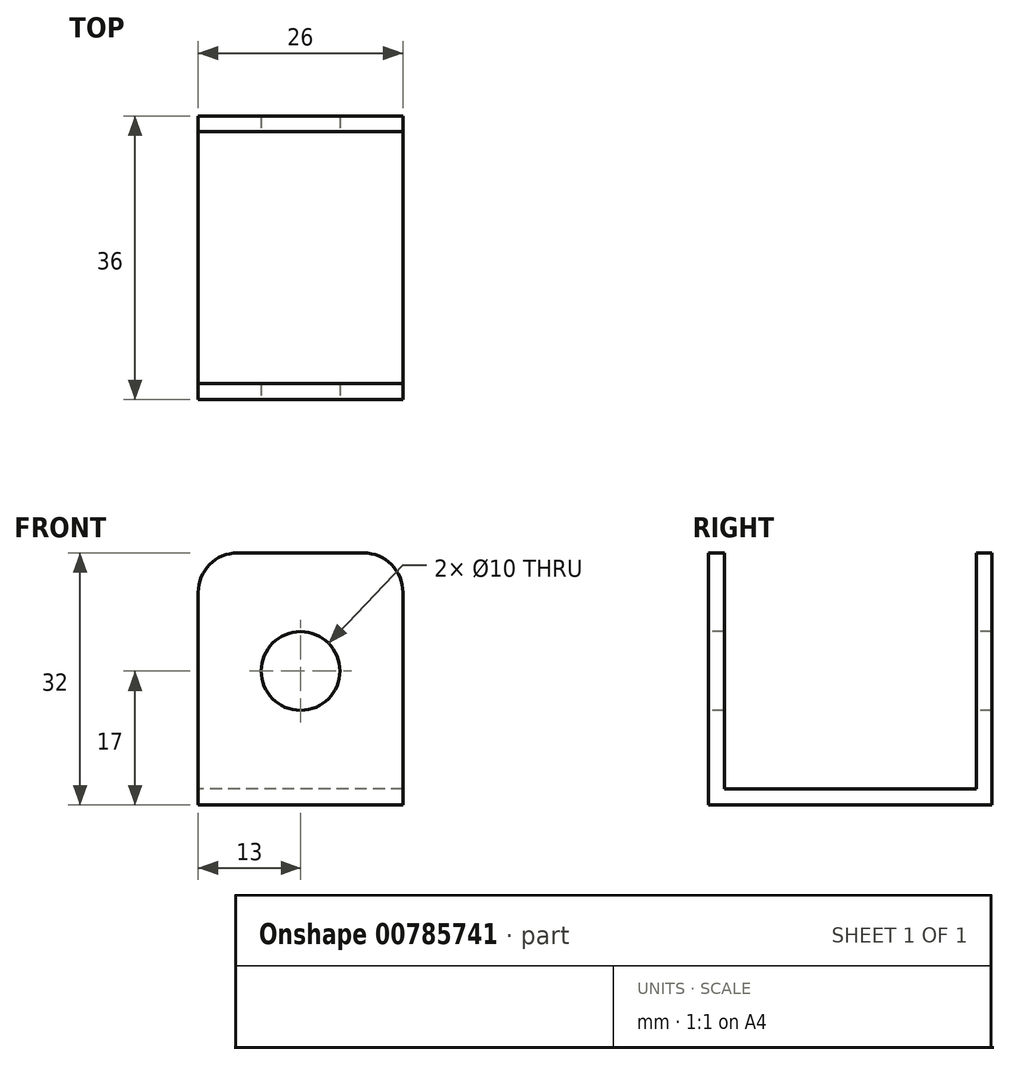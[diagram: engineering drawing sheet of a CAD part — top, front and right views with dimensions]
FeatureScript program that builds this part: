
annotation { "Feature Type Name" : "Feature", "Feature Type Description" : "" }
export const myFeature = defineFeature(function(context is Context, id is Id, definition is map)
    precondition{}
    {
        {
            var Q0;
            Q0=qCreatedBy(makeId("Right.planeOp"),FACE);
            var sketch = newSketch(context, id + "F0", { "sketchPlane" : qUnion([Q0])});
            skLineSegment(sketch, "E0.bottom", {"start": v(-1, 15) * mm, "end": v(1, 15) * mm});
            skLineSegment(sketch, "E0.top", {"start": v(-1, -15) * mm, "end": v(1, -15) * mm});
            skLineSegment(sketch, "E0.left", {"start": v(-1, 15) * mm, "end": v(-1, -15) * mm});
            skLineSegment(sketch, "E0.right", {"start": v(1, 15) * mm, "end": v(1, -15) * mm});
            skPoint(sketch, "E0.middle", {"position": v(0, 0) * mm});
            skLineSegment(sketch, "E1.bottom", {"start": v(-1, -15) * mm, "end": v(35, -15) * mm});
            skLineSegment(sketch, "E1.top", {"start": v(-1, -17) * mm, "end": v(35, -17) * mm});
            skLineSegment(sketch, "E1.left", {"start": v(-1, -15) * mm, "end": v(-1, -17) * mm});
            skLineSegment(sketch, "E1.right", {"start": v(35, -15) * mm, "end": v(35, -17) * mm});
            skLineSegment(sketch, "E2.bottom", {"start": v(35, -15) * mm, "end": v(33, -15) * mm});
            skLineSegment(sketch, "E2.top", {"start": v(35, 15) * mm, "end": v(33, 15) * mm});
            skLineSegment(sketch, "E2.left", {"start": v(35, -15) * mm, "end": v(35, 15) * mm});
            skLineSegment(sketch, "E2.right", {"start": v(33, -15) * mm, "end": v(33, 15) * mm});
            skSolve(sketch);
        }
        {
            var Q0;
            Q0=qSketchRegion(id+"F0",true);
            extrude(context, id + "F1", {"entities" : qUnion([Q0]), "depth" : 26 * mm, "offsetDistance" : 25 * mm});
        }
        {
            var Q0;
            Q0=qCreatedBy(makeId("Front.planeOp"),FACE);
            var sketch = newSketch(context, id + "F2", { "sketchPlane" : qUnion([Q0])});
            skCircle(sketch, "E3", {"center": v(13, 0) * mm, "radius": 5 * mm});
            skSolve(sketch);
        }
        {
            var Q0;
            Q0=qSketchRegion(id+"F2",true);
            extrude(context, id + "F3", {"entities" : qUnion([Q0]), "operationType" : NewBodyOperationType.REMOVE, "oppositeDirection" : true, "depth" : 40.2 * mm, "offsetDistance" : 25 * mm});
        }
        {
            var Q0;
            Q0=qCreatedBy(makeId("Front.planeOp"),FACE);
            var sketch = newSketch(context, id + "F4", { "sketchPlane" : qUnion([Q0])});
            skCircle(sketch, "E4", {"center": v(13, 0) * mm, "radius": 5 * mm});
            skSolve(sketch);
        }
        {
            var Q0;
            Q0=qSketchRegion(id+"F4",true);
            extrude(context, id + "F5", {"entities" : qUnion([Q0]), "operationType" : NewBodyOperationType.REMOVE, "depth" : 23 * mm, "offsetDistance" : 25 * mm});
        }
        {
            var Q0;
            Q0=makeQuery(id+"F1.opExtrude","CAP_EDGE",EDGE,{"disambiguationData":[OSD([sQuery(id+"F0.wireOp",EDGE,"E0.bottom")])],"isStart":false});
            var Q1;
            Q1=makeQuery(id+"F1.opExtrude","CAP_EDGE",EDGE,{"disambiguationData":[OSD([sQuery(id+"F0.wireOp",EDGE,"E2.top")])],"isStart":false});
            var Q2;
            Q2=makeQuery(id+"F1.opExtrude","CAP_EDGE",EDGE,{"disambiguationData":[OSD([sQuery(id+"F0.wireOp",EDGE,"E0.bottom")])],"isStart":true});
            var Q3;
            Q3=makeQuery(id+"F1.opExtrude","CAP_EDGE",EDGE,{"disambiguationData":[OSD([sQuery(id+"F0.wireOp",EDGE,"E2.top")])],"isStart":true});
            fillet(context, id + "F6", {"entities" : qUnion([Q0, Q1, Q2, Q3]), "radius" : 5 * mm, "tangentPropagation" : true, "allowEdgeOverflow" : false});
        }
    });
